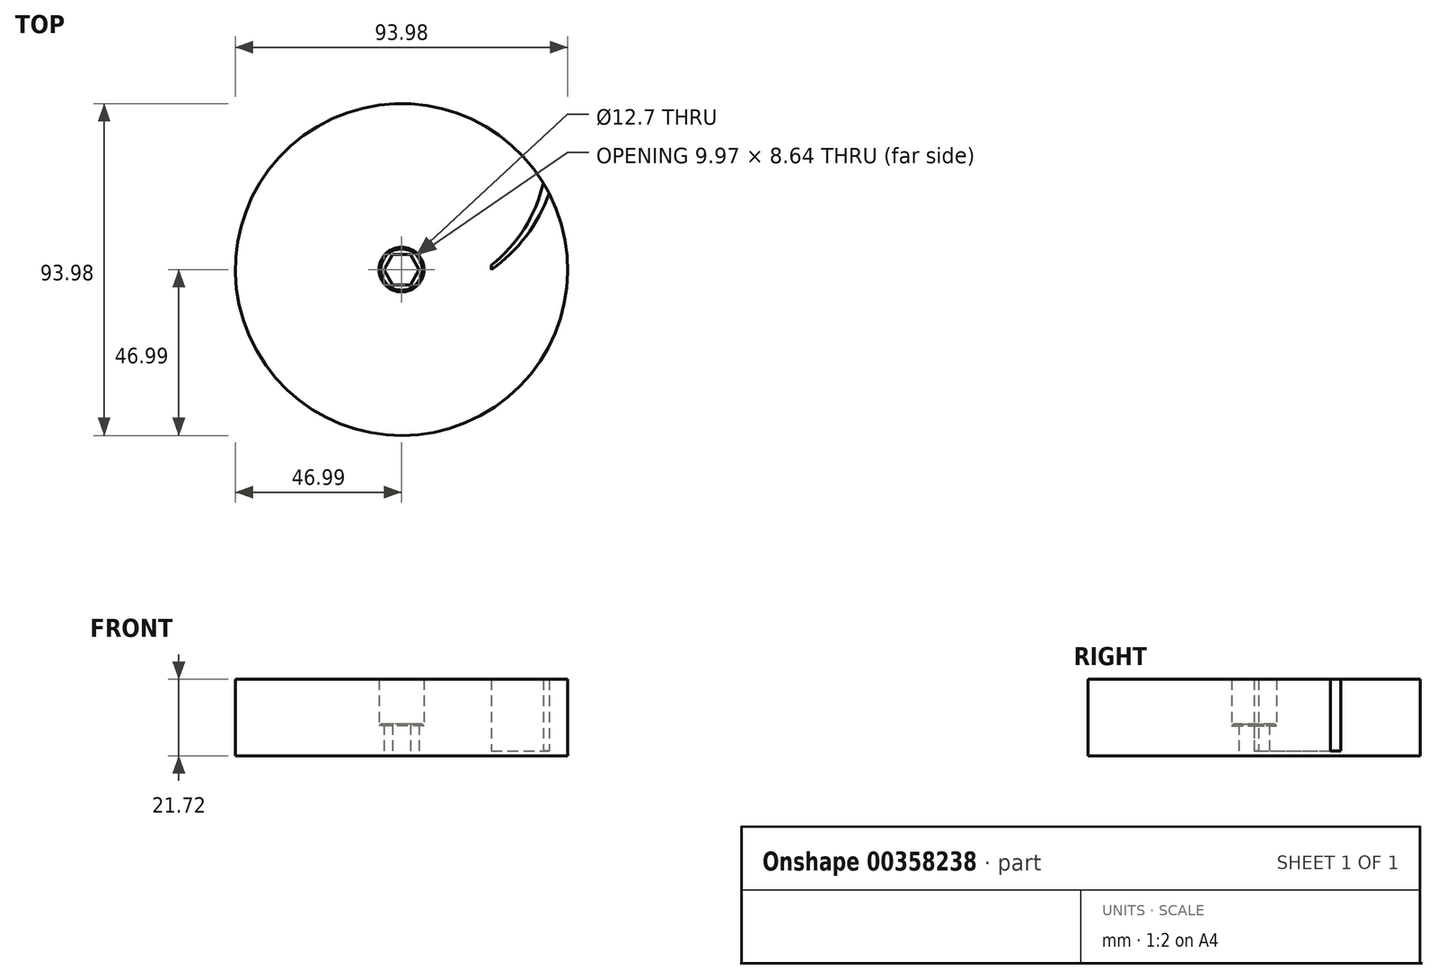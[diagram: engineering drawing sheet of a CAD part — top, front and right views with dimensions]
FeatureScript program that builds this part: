
annotation { "Feature Type Name" : "Feature", "Feature Type Description" : "" }
export const myFeature = defineFeature(function(context is Context, id is Id, definition is map)
    precondition{}
    {
        {
            var Q0;
            Q0=qCreatedBy(makeId("Top.planeOp"),FACE);
            var sketch = newSketch(context, id + "F0", { "sketchPlane" : qUnion([Q0])});
            skCircle(sketch, "E0", {"center": v(0, 0) * mm, "radius": 47 * mm});
            skSolve(sketch);
        }
        {
            var Q0;
            Q0=makeQuery(id+"F0.imprint","IMPRINT",FACE,{"disambiguationData":[TD([[makeQuery(id+"F0.imprint","IMPRINT",EDGE,{"derivedFrom":sQuery(id+"F0.wireOp",EDGE,"E0")}),1.0]])]});
            extrude(context, id + "F1", {"entities" : qUnion([Q0]), "depth" : 1.4 * mm});
        }
        {
            var Q0;
            Q0=makeQuery(id+"F1.opExtrude","CAP_FACE",FACE,{"disambiguationData":[OSD([sQuery(id+"F0.wireOp",EDGE,"E0")])],"isStart":true});
            var sketch = newSketch(context, id + "F2", { "sketchPlane" : qUnion([Q0])});
            skCircle(sketch, "E1.cCircle", {"center": v(0, 0) * mm, "radius": 4.32 * mm, "construction": true});
            skLineSegment(sketch, "E1.0", {"start": v(-2.5, 4.32) * mm, "end": v(2.5, 4.32) * mm});
            skLineSegment(sketch, "E1.1", {"start": v(2.5, 4.32) * mm, "end": v(4.99, 0) * mm});
            skLineSegment(sketch, "E1.2", {"start": v(4.99, 0) * mm, "end": v(2.5, -4.32) * mm});
            skLineSegment(sketch, "E1.3", {"start": v(2.5, -4.32) * mm, "end": v(-2.5, -4.32) * mm});
            skLineSegment(sketch, "E1.4", {"start": v(-2.5, -4.32) * mm, "end": v(-4.99, 0) * mm});
            skLineSegment(sketch, "E1.5", {"start": v(-4.99, 0) * mm, "end": v(-2.5, 4.32) * mm});
            skPoint(sketch, "E1.0.midPoint", {"position": v(0, 4.32) * mm});
            skSolve(sketch);
        }
        {
            var Q0;
            Q0=makeQuery(id+"F2.imprint","IMPRINT",FACE,{"disambiguationData":[TD([[makeQuery(id+"F2.imprint","IMPRINT",EDGE,{"derivedFrom":sQuery(id+"F2.wireOp",EDGE,"E1.0")}),-1.0]])]});
            extrude(context, id + "F3", {"entities" : qUnion([Q0]), "operationType" : NewBodyOperationType.REMOVE, "oppositeDirection" : true, "depth" : 25.4 * mm});
        }
        {
            var Q0;
            Q0=makeQuery(id+"F1.opExtrude","CAP_FACE",FACE,{"disambiguationData":[OSD([sQuery(id+"F0.wireOp",EDGE,"E0")])],"isStart":false});
            var sketch = newSketch(context, id + "F4", { "sketchPlane" : qUnion([Q0])});
            skCircle(sketch, "E2", {"center": v(0, 0) * mm, "radius": 6.35 * mm});
            skSolve(sketch);
        }
        {
            var Q0;
            Q0=makeQuery(id+"F4.imprint","IMPRINT",FACE,{"disambiguationData":[TD([[makeQuery(id+"F4.imprint","IMPRINT",EDGE,{"derivedFrom":sQuery(id+"F4.wireOp",EDGE,"E2")}),1.0]])]});
            extrude(context, id + "F5", {"entities" : qUnion([Q0]), "operationType" : NewBodyOperationType.ADD, "depth" : 7.62 * mm});
        }
        {
            var Q0;
            Q0=makeQuery(id+"F5.opExtrude","CAP_EDGE",EDGE,{"disambiguationData":[OSD([sQuery(id+"F4.wireOp",EDGE,"E2")])],"isStart":false});
            chamfer(context, id + "F6", {"entities" : qUnion([Q0]), "width" : 0.5 * mm, "tangentPropagation" : true});
        }
        {
            var Q0;
            Q0=makeQuery(id+"F1.opExtrude","CAP_FACE",FACE,{"disambiguationData":[OSD([sQuery(id+"F0.wireOp",EDGE,"E0")])],"isStart":false});
            var sketch = newSketch(context, id + "F7", { "sketchPlane" : qUnion([Q0])});
            skCircle(sketch, "E3", {"center": v(0, 0) * mm, "radius": 25.4 * mm, "construction": true});
            skArc(sketch, "E4", {"start": v(41.74, 21.6) * mm, "mid": v(35.26, 9.51) * mm, "end": v(25.4, 0) * mm});
            skLineSegment(sketch, "E5", {"start": v(0, 25.4) * mm, "end": v(0, 47) * mm, "construction": true});
            skArc(sketch, "E6", {"start": v(25.37, 1.27) * mm, "mid": v(34.73, 11.61) * mm, "end": v(40.1, 24.49) * mm});
            skLineSegment(sketch, "E7", {"start": v(25.37, 1.27) * mm, "end": v(25.4, 0) * mm});
            skArc(sketch, "E8.1.0", {"start": v(21.33, 13.78) * mm, "mid": v(24.27, 27.42) * mm, "end": v(22.49, 41.26) * mm});
            skArc(sketch, "E8.1.1", {"start": v(25.35, 39.57) * mm, "mid": v(25.78, 25.87) * mm, "end": v(22, 12.7) * mm});
            skLineSegment(sketch, "E8.1.2", {"start": v(21.33, 13.78) * mm, "end": v(22, 12.7) * mm});
            skArc(sketch, "E8.2.0", {"start": v(11.58, 22.6) * mm, "mid": v(7.31, 35.89) * mm, "end": v(-1.16, 46.98) * mm});
            skArc(sketch, "E8.2.1", {"start": v(2.17, 46.94) * mm, "mid": v(9.4, 35.3) * mm, "end": v(12.7, 22) * mm});
            skLineSegment(sketch, "E8.2.2", {"start": v(11.58, 22.6) * mm, "end": v(12.7, 22) * mm});
            skArc(sketch, "E8.3.0", {"start": v(-1.27, 25.37) * mm, "mid": v(-11.61, 34.73) * mm, "end": v(-24.49, 40.1) * mm});
            skArc(sketch, "E8.3.1", {"start": v(-21.6, 41.74) * mm, "mid": v(-9.51, 35.26) * mm, "end": v(0, 25.4) * mm});
            skLineSegment(sketch, "E8.3.2", {"start": v(-1.27, 25.37) * mm, "end": v(0, 25.4) * mm});
            skArc(sketch, "E8.4.0", {"start": v(-13.78, 21.33) * mm, "mid": v(-27.42, 24.27) * mm, "end": v(-41.26, 22.49) * mm});
            skArc(sketch, "E8.4.1", {"start": v(-39.57, 25.35) * mm, "mid": v(-25.87, 25.78) * mm, "end": v(-12.7, 22) * mm});
            skLineSegment(sketch, "E8.4.2", {"start": v(-13.78, 21.33) * mm, "end": v(-12.7, 22) * mm});
            skArc(sketch, "E8.5.0", {"start": v(-22.6, 11.58) * mm, "mid": v(-35.89, 7.31) * mm, "end": v(-46.98, -1.16) * mm});
            skArc(sketch, "E8.5.1", {"start": v(-46.94, 2.17) * mm, "mid": v(-35.3, 9.4) * mm, "end": v(-22, 12.7) * mm});
            skLineSegment(sketch, "E8.5.2", {"start": v(-22.6, 11.58) * mm, "end": v(-22, 12.7) * mm});
            skArc(sketch, "E8.6.0", {"start": v(-25.37, -1.27) * mm, "mid": v(-34.73, -11.61) * mm, "end": v(-40.1, -24.49) * mm});
            skArc(sketch, "E8.6.1", {"start": v(-41.74, -21.6) * mm, "mid": v(-35.26, -9.51) * mm, "end": v(-25.4, 0) * mm});
            skLineSegment(sketch, "E8.6.2", {"start": v(-25.37, -1.27) * mm, "end": v(-25.4, 0) * mm});
            skArc(sketch, "E8.7.0", {"start": v(-21.33, -13.78) * mm, "mid": v(-24.27, -27.42) * mm, "end": v(-22.49, -41.26) * mm});
            skArc(sketch, "E8.7.1", {"start": v(-25.35, -39.57) * mm, "mid": v(-25.78, -25.87) * mm, "end": v(-22, -12.7) * mm});
            skLineSegment(sketch, "E8.7.2", {"start": v(-21.33, -13.78) * mm, "end": v(-22, -12.7) * mm});
            skArc(sketch, "E8.8.0", {"start": v(-11.58, -22.6) * mm, "mid": v(-7.31, -35.89) * mm, "end": v(1.16, -46.98) * mm});
            skArc(sketch, "E8.8.1", {"start": v(-2.17, -46.94) * mm, "mid": v(-9.4, -35.3) * mm, "end": v(-12.7, -22) * mm});
            skLineSegment(sketch, "E8.8.2", {"start": v(-11.58, -22.6) * mm, "end": v(-12.7, -22) * mm});
            skArc(sketch, "E8.9.0", {"start": v(1.27, -25.37) * mm, "mid": v(11.61, -34.73) * mm, "end": v(24.49, -40.1) * mm});
            skArc(sketch, "E8.9.1", {"start": v(21.6, -41.74) * mm, "mid": v(9.51, -35.26) * mm, "end": v(0, -25.4) * mm});
            skLineSegment(sketch, "E8.9.2", {"start": v(1.27, -25.37) * mm, "end": v(0, -25.4) * mm});
            skArc(sketch, "E8.10.0", {"start": v(13.78, -21.33) * mm, "mid": v(27.42, -24.27) * mm, "end": v(41.26, -22.49) * mm});
            skArc(sketch, "E8.10.1", {"start": v(39.57, -25.35) * mm, "mid": v(25.87, -25.78) * mm, "end": v(12.7, -22) * mm});
            skLineSegment(sketch, "E8.10.2", {"start": v(13.78, -21.33) * mm, "end": v(12.7, -22) * mm});
            skArc(sketch, "E8.11.0", {"start": v(22.6, -11.58) * mm, "mid": v(35.89, -7.31) * mm, "end": v(46.98, 1.16) * mm});
            skArc(sketch, "E8.11.1", {"start": v(46.94, -2.17) * mm, "mid": v(35.3, -9.4) * mm, "end": v(22, -12.7) * mm});
            skLineSegment(sketch, "E8.11.2", {"start": v(22.6, -11.58) * mm, "end": v(22, -12.7) * mm});
            skSolve(sketch);
        }
        {
            var Q0;
            {var subQ0=sQuery(id+"F7.wireOp",EDGE,"E4");Q0=makeQuery(id+"F7.imprint","IMPRINT",FACE,{"disambiguationData":[TD([[makeQuery(id+"F7.imprint","IMPRINT",EDGE,{"derivedFrom":subQ0}),-1.0]])]});}
            var Q1;
            {var subQ0=sQuery(id+"F7.wireOp",EDGE,"E8.1.0");Q1=makeQuery(id+"F7.imprint","IMPRINT",FACE,{"disambiguationData":[TD([[makeQuery(id+"F7.imprint","IMPRINT",EDGE,{"derivedFrom":subQ0}),-1.0]])]});}
            var Q2;
            {var subQ0=sQuery(id+"F7.wireOp",EDGE,"E8.2.0");Q2=makeQuery(id+"F7.imprint","IMPRINT",FACE,{"disambiguationData":[TD([[makeQuery(id+"F7.imprint","IMPRINT",EDGE,{"derivedFrom":subQ0}),-1.0]])]});}
            var Q3;
            {var subQ0=sQuery(id+"F7.wireOp",EDGE,"E8.3.0");Q3=makeQuery(id+"F7.imprint","IMPRINT",FACE,{"disambiguationData":[TD([[makeQuery(id+"F7.imprint","IMPRINT",EDGE,{"derivedFrom":subQ0}),-1.0]])]});}
            var Q4;
            {var subQ0=sQuery(id+"F7.wireOp",EDGE,"E8.4.0");Q4=makeQuery(id+"F7.imprint","IMPRINT",FACE,{"disambiguationData":[TD([[makeQuery(id+"F7.imprint","IMPRINT",EDGE,{"derivedFrom":subQ0}),-1.0]])]});}
            var Q5;
            {var subQ0=sQuery(id+"F7.wireOp",EDGE,"E8.5.0");Q5=makeQuery(id+"F7.imprint","IMPRINT",FACE,{"disambiguationData":[TD([[makeQuery(id+"F7.imprint","IMPRINT",EDGE,{"derivedFrom":subQ0}),-1.0]])]});}
            var Q6;
            {var subQ0=sQuery(id+"F7.wireOp",EDGE,"E8.6.0");Q6=makeQuery(id+"F7.imprint","IMPRINT",FACE,{"disambiguationData":[TD([[makeQuery(id+"F7.imprint","IMPRINT",EDGE,{"derivedFrom":subQ0}),-1.0]])]});}
            var Q7;
            {var subQ0=sQuery(id+"F7.wireOp",EDGE,"E8.7.0");Q7=makeQuery(id+"F7.imprint","IMPRINT",FACE,{"disambiguationData":[TD([[makeQuery(id+"F7.imprint","IMPRINT",EDGE,{"derivedFrom":subQ0}),-1.0]])]});}
            var Q8;
            {var subQ0=sQuery(id+"F7.wireOp",EDGE,"E8.8.0");Q8=makeQuery(id+"F7.imprint","IMPRINT",FACE,{"disambiguationData":[TD([[makeQuery(id+"F7.imprint","IMPRINT",EDGE,{"derivedFrom":subQ0}),-1.0]])]});}
            var Q9;
            {var subQ0=sQuery(id+"F7.wireOp",EDGE,"E8.9.0");Q9=makeQuery(id+"F7.imprint","IMPRINT",FACE,{"disambiguationData":[TD([[makeQuery(id+"F7.imprint","IMPRINT",EDGE,{"derivedFrom":subQ0}),-1.0]])]});}
            var Q10;
            {var subQ0=sQuery(id+"F7.wireOp",EDGE,"E8.10.0");Q10=makeQuery(id+"F7.imprint","IMPRINT",FACE,{"disambiguationData":[TD([[makeQuery(id+"F7.imprint","IMPRINT",EDGE,{"derivedFrom":subQ0}),-1.0]])]});}
            var Q11;
            {var subQ0=sQuery(id+"F7.wireOp",EDGE,"E8.11.0");Q11=makeQuery(id+"F7.imprint","IMPRINT",FACE,{"disambiguationData":[TD([[makeQuery(id+"F7.imprint","IMPRINT",EDGE,{"derivedFrom":subQ0}),-1.0]])]});}
            extrude(context, id + "F8", {"entities" : qUnion([Q0, Q1, Q2, Q3, Q4, Q5, Q6, Q7, Q8, Q9, Q10, Q11]), "operationType" : NewBodyOperationType.ADD, "depth" : 20.32 * mm});
        }
    });
